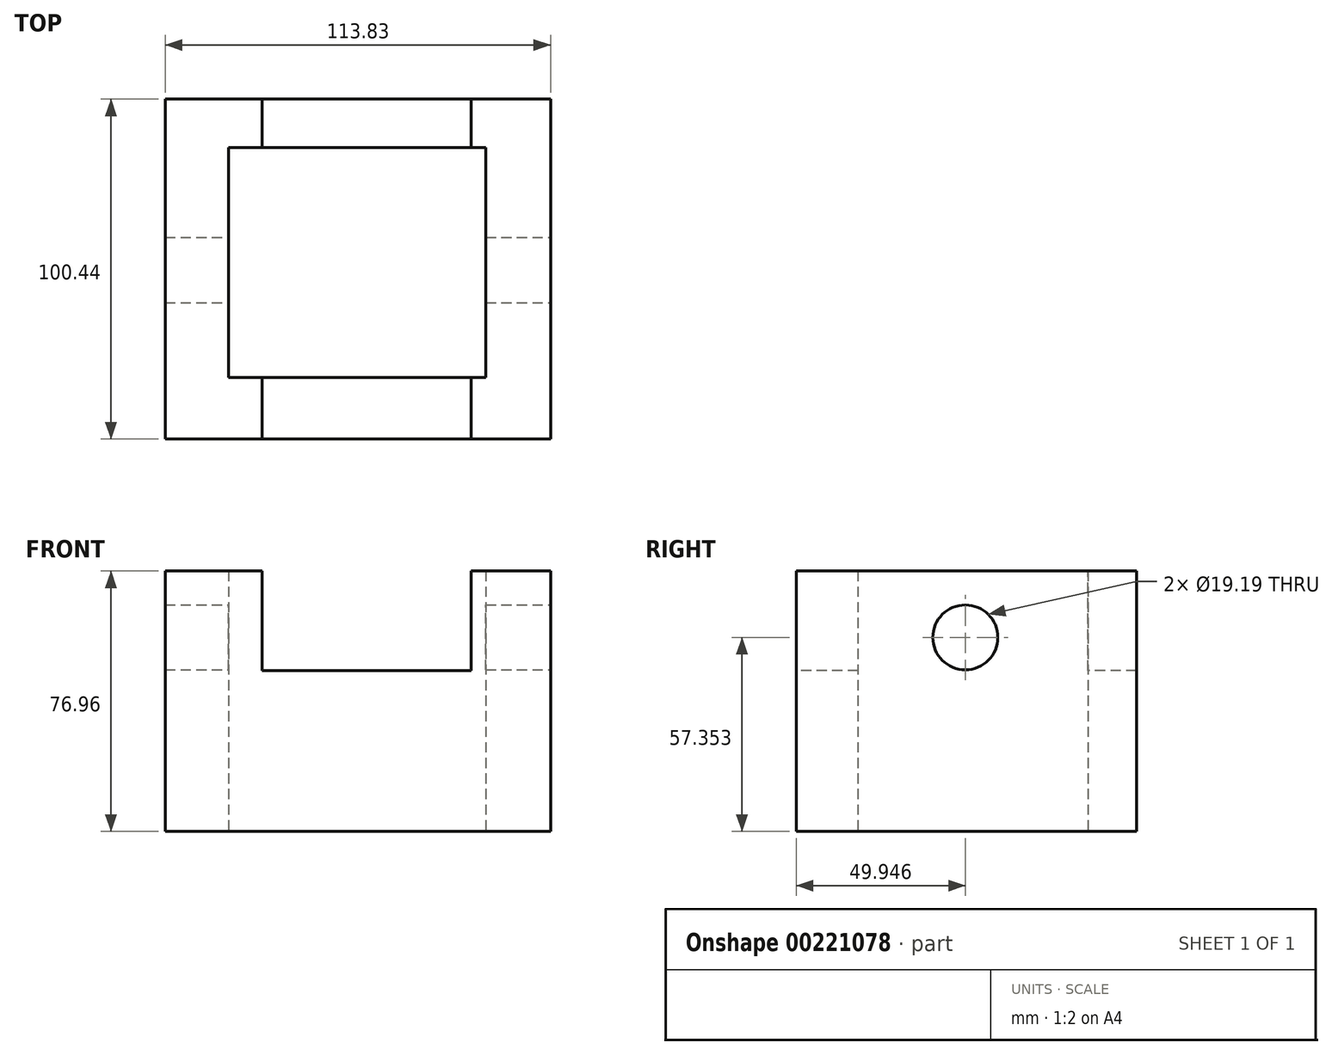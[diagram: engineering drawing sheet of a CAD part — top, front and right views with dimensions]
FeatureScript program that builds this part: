
annotation { "Feature Type Name" : "Feature", "Feature Type Description" : "" }
export const myFeature = defineFeature(function(context is Context, id is Id, definition is map)
    precondition{}
    {
        {
            var Q0;
            Q0=qCreatedBy(makeId("Top.planeOp"),FACE);
            var sketch = newSketch(context, id + "F0", { "sketchPlane" : qUnion([Q0])});
            skLineSegment(sketch, "E0.bottom", {"start": v(-46.87, 42.14) * mm, "end": v(66.96, 42.14) * mm});
            skLineSegment(sketch, "E0.top", {"start": v(-46.87, -32.9) * mm, "end": v(66.96, -32.9) * mm});
            skLineSegment(sketch, "E0.left", {"start": v(-46.87, 42.14) * mm, "end": v(-46.87, -32.9) * mm});
            skLineSegment(sketch, "E0.right", {"start": v(66.96, 42.14) * mm, "end": v(66.96, -32.9) * mm});
            skLineSegment(sketch, "E1.bottom", {"start": v(-28.17, 27.82) * mm, "end": v(47.8, 27.82) * mm});
            skLineSegment(sketch, "E1.top", {"start": v(-28.17, -19.74) * mm, "end": v(47.8, -19.74) * mm});
            skLineSegment(sketch, "E1.left", {"start": v(-28.17, 27.82) * mm, "end": v(-28.17, -19.74) * mm});
            skLineSegment(sketch, "E1.right", {"start": v(47.8, 27.82) * mm, "end": v(47.8, -19.74) * mm});
            skSolve(sketch);
        }
        {
            var Q0;
            Q0 = qSketchRegion(id + "F0", true);
            extrude(context, id + "F1", {"entities" : qUnion([Q0]), "depth" : 76.96 * mm});
        }
        {
            var Q0;
            Q0=makeQuery(id+"F1.opExtrude","SWEPT_FACE",FACE,{"disambiguationData":[OSD([sQuery(id+"F0.wireOp",EDGE,"E0.top")])]});
            extrude(context, id + "F2", {"entities" : qUnion([Q0]), "operationType" : NewBodyOperationType.ADD, "depth" : 25.4 * mm});
        }
        {
            var Q0;
            Q0=makeQuery(id+"F2.opExtrude","CAP_FACE",FACE,{"disambiguationData":[OSD([sQuery(id+"F0.wireOp",EDGE,"E0.top")])],"isStart":false});
            var sketch = newSketch(context, id + "F3", { "sketchPlane" : qUnion([Q0])});
            skLineSegment(sketch, "E2.bottom", {"start": v(-18.25, 76.96) * mm, "end": v(43.44, 76.96) * mm});
            skLineSegment(sketch, "E2.top", {"start": v(-18.25, 47.58) * mm, "end": v(43.44, 47.58) * mm});
            skLineSegment(sketch, "E2.left", {"start": v(-18.25, 76.96) * mm, "end": v(-18.25, 47.58) * mm});
            skLineSegment(sketch, "E2.right", {"start": v(43.44, 76.96) * mm, "end": v(43.44, 47.58) * mm});
            skSolve(sketch);
        }
        {
            var Q0;
            Q0 = qSketchRegion(id + "F3", true);
            extrude(context, id + "F4", {"entities" : qUnion([Q0]), "operationType" : NewBodyOperationType.REMOVE, "oppositeDirection" : true, "depth" : 132.84 * mm});
        }
        {
            var Q0;
            Q0=qCreatedBy(makeId("Top.planeOp"),FACE);
            var sketch = newSketch(context, id + "F5", { "sketchPlane" : qUnion([Q0])});
            skLineSegment(sketch, "E3.bottom", {"start": v(-28.17, 27.6) * mm, "end": v(47.8, 27.6) * mm});
            skLineSegment(sketch, "E3.top", {"start": v(-28.17, -40.06) * mm, "end": v(47.8, -40.06) * mm});
            skLineSegment(sketch, "E3.left", {"start": v(-28.17, 27.6) * mm, "end": v(-28.17, -40.06) * mm});
            skLineSegment(sketch, "E3.right", {"start": v(47.8, 27.6) * mm, "end": v(47.8, -40.06) * mm});
            skSolve(sketch);
        }
        {
            var Q0;
            Q0 = qSketchRegion(id + "F5", true);
            extrude(context, id + "F6", {"entities" : qUnion([Q0]), "operationType" : NewBodyOperationType.REMOVE, "depth" : 129.03 * mm});
        }
        {
            var Q0;
            {var subQ0=sQuery(id+"F0.wireOp",EDGE,"E0.right");Q0=makeQuery(id+"F2.boolean.opBoolean","MERGE",FACE,{"derivedFrom":[makeQuery(id+"F1.opExtrude","SWEPT_FACE",FACE,{"disambiguationData":[OSD([subQ0])]}),makeQuery(id+"F2.opExtrude","SWEPT_FACE",FACE,{"disambiguationData":[OSD([sQuery(id+"F0.wireOp",EDGE,"E0.top"),subQ0])]})]});}
            var sketch = newSketch(context, id + "F7", { "sketchPlane" : qUnion([Q0])});
            skCircle(sketch, "E4", {"center": v(-8.35, 57.35) * mm, "radius": 9.6 * mm});
            skSolve(sketch);
        }
        {
            var Q0;
            Q0 = qSketchRegion(id + "F7", true);
            extrude(context, id + "F8", {"entities" : qUnion([Q0]), "operationType" : NewBodyOperationType.REMOVE, "oppositeDirection" : true, "depth" : 241.8 * mm});
        }
    });
